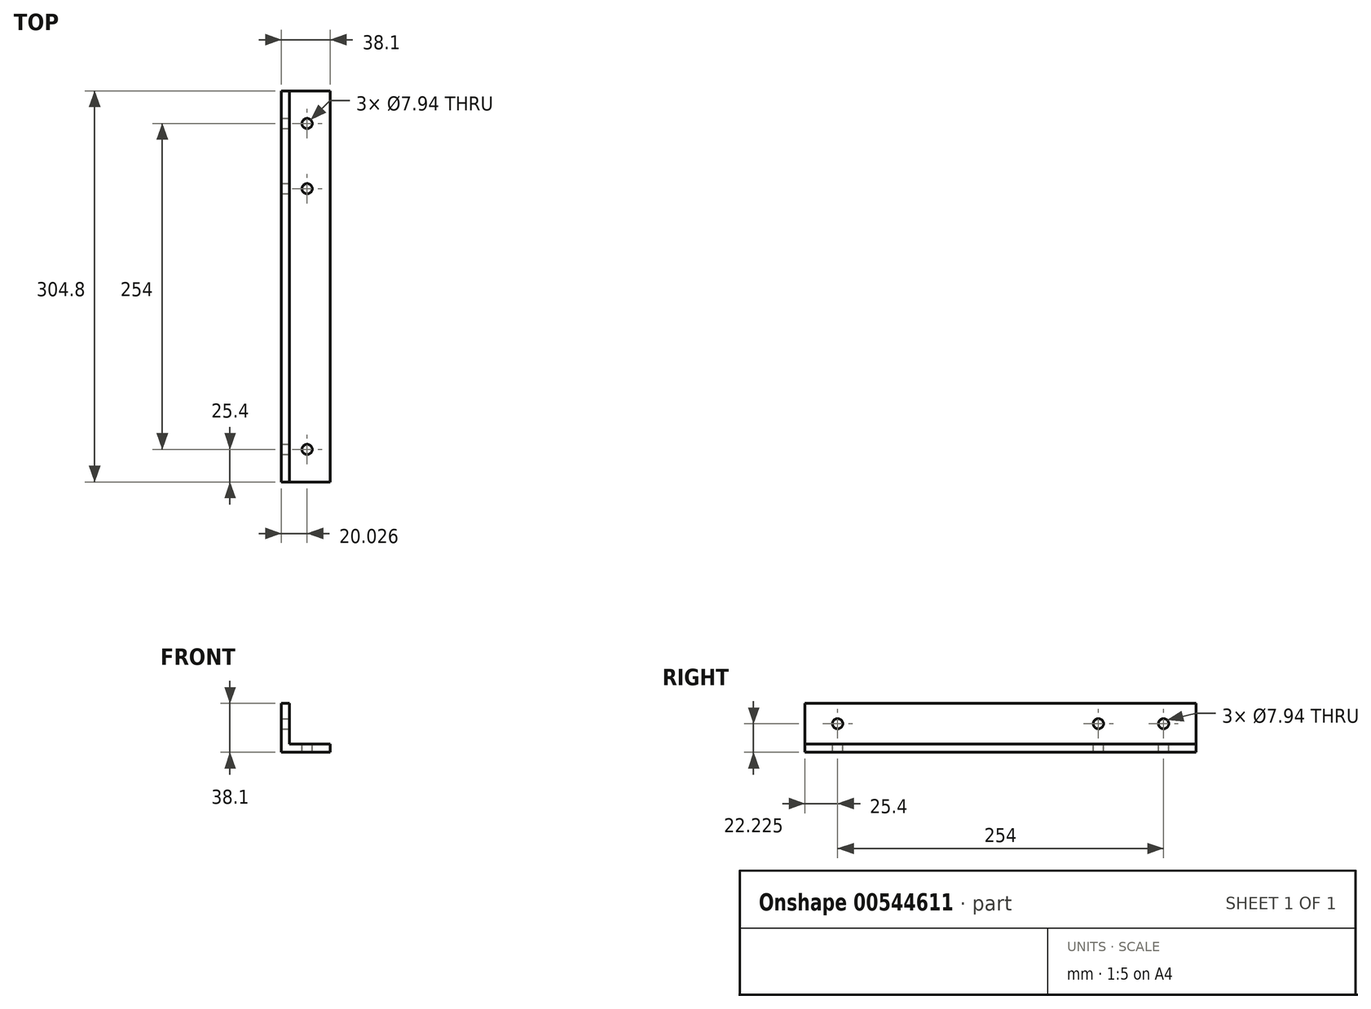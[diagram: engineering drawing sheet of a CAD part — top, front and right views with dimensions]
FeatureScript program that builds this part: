
annotation { "Feature Type Name" : "Feature", "Feature Type Description" : "" }
export const myFeature = defineFeature(function(context is Context, id is Id, definition is map)
    precondition{}
    {
        {
            var Q0;
            Q0=qCreatedBy(makeId("Front.planeOp"),FACE);
            var sketch = newSketch(context, id + "F0", { "sketchPlane" : qUnion([Q0])});
            skLineSegment(sketch, "E0", {"start": v(0, 0) * mm, "end": v(0, 38.1) * mm});
            skLineSegment(sketch, "E1", {"start": v(0, 38.1) * mm, "end": v(6.35, 38.1) * mm});
            skLineSegment(sketch, "E2.0", {"start": v(6.35, 6.35) * mm, "end": v(6.35, 38.1) * mm});
            skLineSegment(sketch, "E3", {"start": v(0, 0) * mm, "end": v(38.1, 0) * mm});
            skLineSegment(sketch, "E4", {"start": v(38.1, 0) * mm, "end": v(38.1, 6.35) * mm});
            skLineSegment(sketch, "E5", {"start": v(38.1, 6.35) * mm, "end": v(6.35, 6.35) * mm});
            skSolve(sketch);
        }
        {
            var Q0;
            Q0=makeQuery(id+"F0.imprint","IMPRINT",FACE,{"disambiguationData":[TD([[makeQuery(id+"F0.imprint","IMPRINT",EDGE,{"derivedFrom":sQuery(id+"F0.wireOp",EDGE,"E0")}),-1.0]])]});
            extrude(context, id + "F1", {"entities" : qUnion([Q0]), "endBound" : BoundingType.SYMMETRIC, "depth" : 304.8 * mm, "offsetDistance" : 25.4 * mm});
        }
        {
            var Q0;
            Q0=makeQuery(id+"F1.opExtrude","SWEPT_FACE",FACE,{"disambiguationData":[OSD([sQuery(id+"F0.wireOp",EDGE,"E5")])]});
            var sketch = newSketch(context, id + "F2", { "sketchPlane" : qUnion([Q0])});
            skPoint(sketch, "E6", {"position": v(20.03, -127) * mm});
            skPoint(sketch, "E7", {"position": v(20.03, 76.2) * mm});
            skPoint(sketch, "E8", {"position": v(20.03, 127) * mm});
            skSolve(sketch);
        }
        {
            var Q0;
            Q0=sQuery(id+"F2.wireOp",VERTEX,"E6");
            var Q1;
            Q1=sQuery(id+"F2.wireOp",VERTEX,"E7");
            var Q2;
            Q2=sQuery(id+"F2.wireOp",VERTEX,"E8");
            var Q3;
            Q3=makeQuery(id+"F1.opExtrude","SWEPT_BODY",BODY,{"disambiguationData":[OSD([sQuery(id+"F0.wireOp",EDGE,"E0"),sQuery(id+"F0.wireOp",EDGE,"E1"),sQuery(id+"F0.wireOp",EDGE,"E2.0"),sQuery(id+"F0.wireOp",EDGE,"E3"),sQuery(id+"F0.wireOp",EDGE,"E4"),sQuery(id+"F0.wireOp",EDGE,"E5")])]});
            hole(context, id + "F3", {"style" : HoleStyle.SIMPLE, "endStyle" : HoleEndStyle.THROUGH, "holeDiameter" : 7.94 * mm, "majorDiameter" : 6.35 * mm, "isTappedThrough" : true, "tappedDepth" : 12.7 * mm, "tapClearance" : 3, "locations" : qUnion([Q0, Q1, Q2]), "scope" : qUnion([Q3])});
        }
        {
            var Q0;
            Q0=makeQuery(id+"F1.opExtrude","SWEPT_FACE",FACE,{"disambiguationData":[OSD([sQuery(id+"F0.wireOp",EDGE,"E2.0")])]});
            var sketch = newSketch(context, id + "F4", { "sketchPlane" : qUnion([Q0])});
            skPoint(sketch, "E9", {"position": v(-127, 22.22) * mm});
            skPoint(sketch, "E10", {"position": v(76.2, 22.23) * mm});
            skPoint(sketch, "E11", {"position": v(127, 22.23) * mm});
            skSolve(sketch);
        }
        {
            var Q0;
            Q0=sQuery(id+"F4.wireOp",VERTEX,"E9");
            var Q1;
            Q1=sQuery(id+"F4.wireOp",VERTEX,"E10");
            var Q2;
            Q2=sQuery(id+"F4.wireOp",VERTEX,"E11");
            var Q3;
            Q3=makeQuery(id+"F1.opExtrude","SWEPT_BODY",BODY,{"disambiguationData":[OSD([sQuery(id+"F0.wireOp",EDGE,"E0"),sQuery(id+"F0.wireOp",EDGE,"E1"),sQuery(id+"F0.wireOp",EDGE,"E2.0"),sQuery(id+"F0.wireOp",EDGE,"E3"),sQuery(id+"F0.wireOp",EDGE,"E4"),sQuery(id+"F0.wireOp",EDGE,"E5")])]});
            hole(context, id + "F5", {"style" : HoleStyle.SIMPLE, "endStyle" : HoleEndStyle.THROUGH, "holeDiameter" : 7.94 * mm, "majorDiameter" : 6.35 * mm, "isTappedThrough" : true, "tappedDepth" : 12.7 * mm, "tapClearance" : 3, "locations" : qUnion([Q0, Q1, Q2]), "scope" : qUnion([Q3])});
        }
    });
